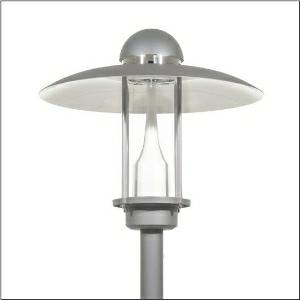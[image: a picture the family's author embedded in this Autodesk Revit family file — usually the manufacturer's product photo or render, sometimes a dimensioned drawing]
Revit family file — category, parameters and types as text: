
# Revit family: city-light_elegance_iq___st1_2a_5xa5265kf14h_1fe5
name_source: partatom
category: Lighting Fixtures
units: mm (PartAtom-declared; Revit-internal decimal feet)

## family parameters
Cut with Voids When Loaded = No
Host = Face
Light Source = No
Part Type = Normal
Room Calculation Point = No
Round Connector Dimension = Use Diameter
Shared = No

## types (1)
- --- (1 x LED, 1470 lm, 10 W, 4000K)
    Apparent Load = 10 VA
    CIE Flux Codes = 22 62 94 98 100
    Color Rendering = 70
    Color Temperature = 4000K
    Default Elevation = 1800 mm
    Description = City-Light Elegance iQ, mast luminaire, Module 540 iQ-SR, primary light control with 3 zone facetted reflector, of plastic, silver coated, highly specular, structured, primary optical cover: cover, of PMMA, transparent, light distribution: ST1.2a, light emission: direct distribution, primary light characteristic: asymmetric, installation type: post-top, LED, High Power LED, rated luminous flux: 1.470lm, luminous efficacy: 147lm/W, light colour: 740, colour temperature: 4000K, control gear: iQ Street-Remote, control: pre-setting: logarithmic dimming characteristic, Street-Remote, Auto-Match, Temp-Guard, Lumen-Switch, Night-Set, Smart-Wire, Light-Fading, Desk-Remote (wireless, voltage-free reading and setting of iQ features in the workshop via application-optimized NFC function/RFID function), optimised constant luminous flux control (CLO 2.0), with terminal, 6-pole, max. 2.5mm², mains connection: 230..240V, AC, 50/60Hz, start of lifetime: 10W, end of service life: 10W, reduction: 5W, luminaire housing, upper part, of aluminium, coated, Siteco® metallic grey (DB 702S), diameter: 750mm, height: 675mm, spigot size: d x l = 76 x 70mm (post-top) | with reducer (optional accessory) 60 x 70mm, mounting height: 3..5m, post-top mast mounting element, of diecast aluminium, coated, Siteco® metallic grey (DB 702S), Module 540 iQ-SR, traffic white (RAL 9016), equipment: standard, protection rating (complete): IP65, insulation class (complete): insulation class II (safety insulation), certification: CE, ENEC, VDE, packaging unit: 1 piece

Light Distribution: ST1.2a
    Height = 675 mm
    Lamp = 1 x LED
    Lamp Light Flux = 1470 lm
    Lamp Power = 10 W
    Lamp count = 1
    Length = 750 mm
    Luminous efficacy = 147 lm/W
    Manufacturer = Siteco
    ModVariant = No
    Model = 5XA5265KF14H
    Number of Poles = 1
    OnlyDefault = Yes
    Power Factor = 1
    Product Name = City-Light Elegance iQ | ST1.2a
    Product group = mast luminaire | pylon top
    ProductGroupID = 6100
    Protection Class = Protection class II
    Protection Degree = IP 65
    RLX_Detail_Level = 1
    RLX_Emergency_Light_Flux = 0 lm
    RLX_Emergency_Type = 0
    RLX_Emergency_Type_DB = No
    RlxData = <blob elided: 103901 chars, md5=19cf603b>
    Socket = socket
    Standby Power = 0 W
    System Light Flux = 1470 lm
    System Power = 10 W
    Type Comments = factory setting: luminous flux: 100 % | dim-lin: 254 | 401 mA
    Type Image = l_1006912.jpg
    URL = http://relux.com
    VarID = @adj_181289
    Voltage = 0 V
    Weight = 0.00 kg
    Width = 0 mm  [stored 0 ft]

note: [stored X ft] marks values corroborated as IEEE doubles in the binary element streams (Revit-internal decimal feet)

## geometry (parser evidence)
native form markers: Blend x4, Sweep x12
no freeform markers — native parametric forms only
